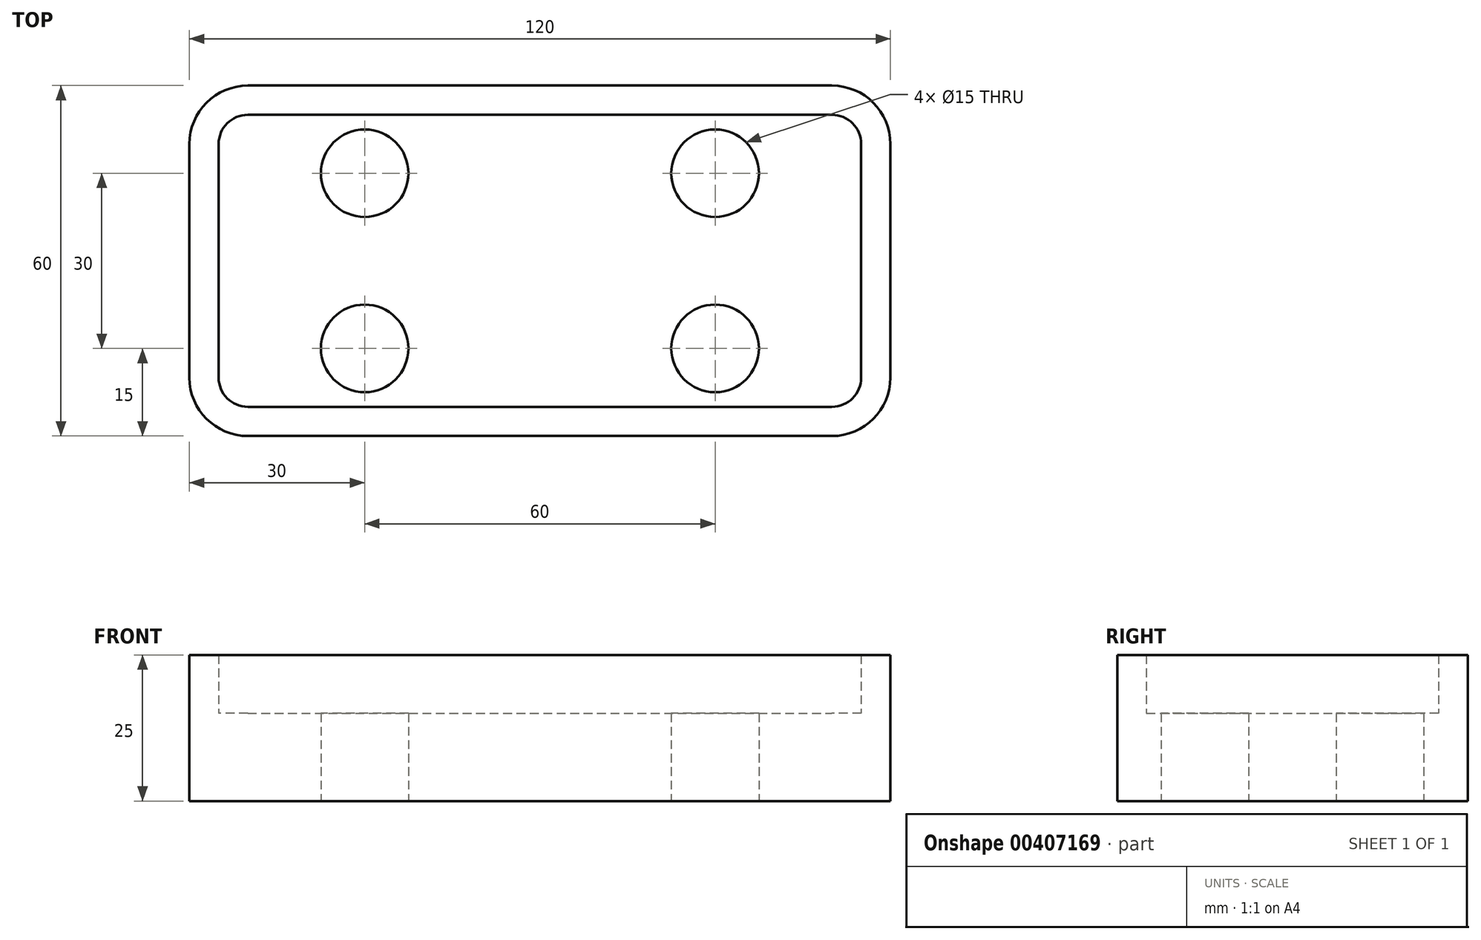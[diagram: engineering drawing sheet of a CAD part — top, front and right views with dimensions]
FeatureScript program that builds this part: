
annotation { "Feature Type Name" : "Feature", "Feature Type Description" : "" }
export const myFeature = defineFeature(function(context is Context, id is Id, definition is map)
    precondition{}
    {
        {
            var Q0;
            Q0=qCreatedBy(makeId("Top.planeOp"),FACE);
            var sketch = newSketch(context, id + "F0", { "sketchPlane" : qUnion([Q0])});
            skLineSegment(sketch, "E0.bottom", {"start": v(-50, -30) * mm, "end": v(50, -30) * mm});
            skLineSegment(sketch, "E0.top", {"start": v(-50, 30) * mm, "end": v(50, 30) * mm});
            skLineSegment(sketch, "E0.left", {"start": v(-60, -20) * mm, "end": v(-60, 20) * mm});
            skLineSegment(sketch, "E0.right", {"start": v(60, -20) * mm, "end": v(60, 20) * mm});
            skPoint(sketch, "E0.middle", {"position": v(0, 0) * mm});
            skCircle(sketch, "E1", {"center": v(-30, -15) * mm, "radius": 7.5 * mm});
            skCircle(sketch, "E2.0.1.0", {"center": v(-30, 15) * mm, "radius": 7.5 * mm});
            skCircle(sketch, "E2.1.0.0", {"center": v(30, -15) * mm, "radius": 7.5 * mm});
            skCircle(sketch, "E2.1.1.0", {"center": v(30, 15) * mm, "radius": 7.5 * mm});
            skLineSegment(sketch, "E2.direction1", {"start": v(-30, -15) * mm, "end": v(30, -15) * mm, "construction": true});
            skLineSegment(sketch, "E2.direction2", {"start": v(-30, -15) * mm, "end": v(-30, 15) * mm, "construction": true});
            skPoint(sketch, "E3.visualSharp", {"position": v(-60, 30) * mm});
            skArc(sketch, "E3.filletArc", {"start": v(-50, 30) * mm, "mid": v(-57.07, 27.07) * mm, "end": v(-60, 20) * mm});
            skPoint(sketch, "E4.visualSharp", {"position": v(60, 30) * mm});
            skArc(sketch, "E4.filletArc", {"start": v(60, 20) * mm, "mid": v(57.07, 27.07) * mm, "end": v(50, 30) * mm});
            skPoint(sketch, "E5.visualSharp", {"position": v(60, -30) * mm});
            skArc(sketch, "E5.filletArc", {"start": v(50, -30) * mm, "mid": v(57.07, -27.07) * mm, "end": v(60, -20) * mm});
            skPoint(sketch, "E6.visualSharp", {"position": v(-60, -30) * mm});
            skArc(sketch, "E6.filletArc", {"start": v(-60, -20) * mm, "mid": v(-57.07, -27.07) * mm, "end": v(-50, -30) * mm});
            skArc(sketch, "E7.0", {"start": v(-50, 25) * mm, "mid": v(-53.54, 23.54) * mm, "end": v(-55, 20) * mm});
            skLineSegment(sketch, "E7.1", {"start": v(-55, -20) * mm, "end": v(-55, 20) * mm});
            skLineSegment(sketch, "E7.2", {"start": v(-50, 25) * mm, "end": v(50, 25) * mm});
            skArc(sketch, "E7.3", {"start": v(-55, -20) * mm, "mid": v(-53.54, -23.54) * mm, "end": v(-50, -25) * mm});
            skArc(sketch, "E7.4", {"start": v(55, 20) * mm, "mid": v(53.54, 23.54) * mm, "end": v(50, 25) * mm});
            skLineSegment(sketch, "E7.5", {"start": v(55, -20) * mm, "end": v(55, 20) * mm});
            skArc(sketch, "E7.6", {"start": v(50, -25) * mm, "mid": v(53.54, -23.54) * mm, "end": v(55, -20) * mm});
            skLineSegment(sketch, "E7.7", {"start": v(-50, -25) * mm, "end": v(50, -25) * mm});
            skSolve(sketch);
        }
        {
            var Q0;
            Q0=makeQuery(id+"F0.imprint","IMPRINT",FACE,{"disambiguationData":[TD([[makeQuery(id+"F0.imprint","IMPRINT",EDGE,{"derivedFrom":sQuery(id+"F0.wireOp",EDGE,"E0.bottom")}),1.0]])]});
            extrude(context, id + "F1", {"entities" : qUnion([Q0]), "depth" : 25 * mm});
        }
        {
            var Q0;
            Q0=makeQuery(id+"F0.imprint","IMPRINT",FACE,{"disambiguationData":[TD([[makeQuery(id+"F0.imprint","IMPRINT",EDGE,{"derivedFrom":sQuery(id+"F0.wireOp",EDGE,"E1")}),-1.0]])]});
            extrude(context, id + "F2", {"entities" : qUnion([Q0]), "operationType" : NewBodyOperationType.ADD, "depth" : 15 * mm});
        }
    });
